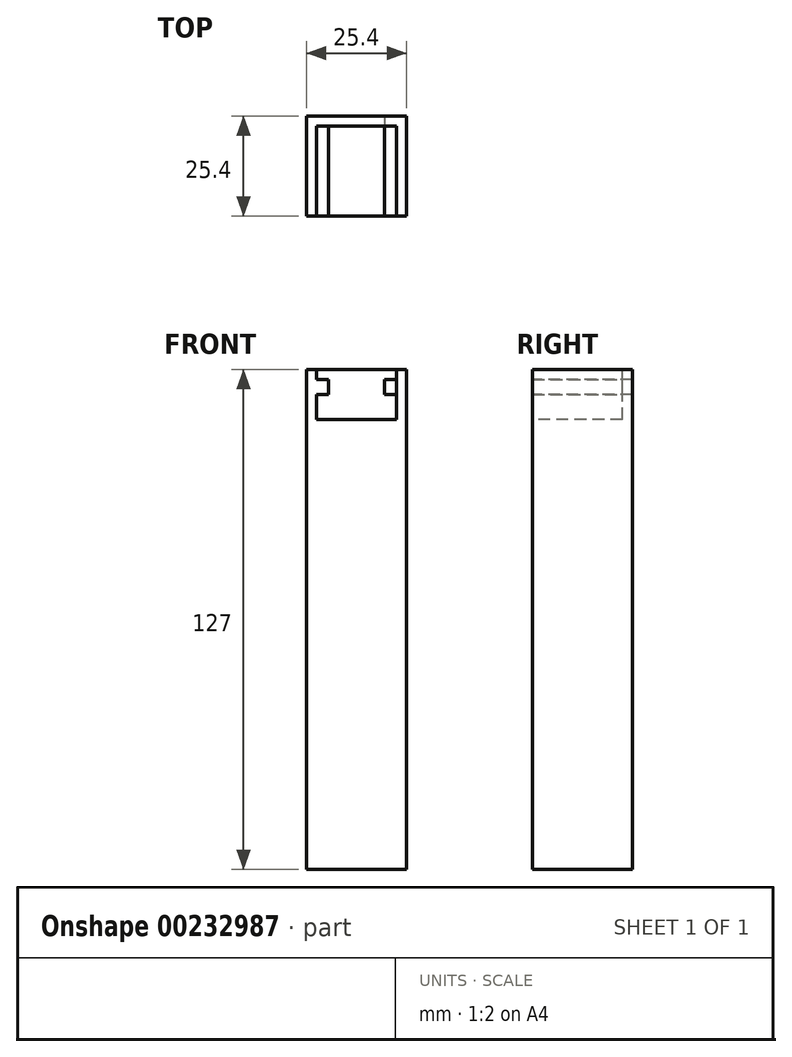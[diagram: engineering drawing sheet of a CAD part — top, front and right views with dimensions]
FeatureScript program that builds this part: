
annotation { "Feature Type Name" : "Feature", "Feature Type Description" : "" }
export const myFeature = defineFeature(function(context is Context, id is Id, definition is map)
    precondition{}
    {
        {
            var Q0;
            Q0=qCreatedBy(makeId("Top.planeOp"),FACE);
            var sketch = newSketch(context, id + "F0", { "sketchPlane" : qUnion([Q0])});
            skLineSegment(sketch, "E0.bottom", {"start": v(0, 0) * mm, "end": v(25.4, 0) * mm});
            skLineSegment(sketch, "E0.top", {"start": v(0, 25.4) * mm, "end": v(25.4, 25.4) * mm});
            skLineSegment(sketch, "E0.left", {"start": v(0, 0) * mm, "end": v(0, 25.4) * mm});
            skLineSegment(sketch, "E0.right", {"start": v(25.4, 0) * mm, "end": v(25.4, 25.4) * mm});
            skSolve(sketch);
        }
        {
            var Q0;
            Q0=makeQuery(id+"F0.imprint","IMPRINT",FACE,{"disambiguationData":[TD([[makeQuery(id+"F0.imprint","IMPRINT",EDGE,{"derivedFrom":sQuery(id+"F0.wireOp",EDGE,"E0.bottom")}),1.0]])]});
            extrude(context, id + "F1", {"entities" : qUnion([Q0]), "oppositeDirection" : true, "depth" : 127 * mm});
        }
        {
            var Q0;
            Q0=makeQuery(id+"F1.opExtrude","CAP_FACE",FACE,{"disambiguationData":[OSD([sQuery(id+"F0.wireOp",EDGE,"E0.bottom"),sQuery(id+"F0.wireOp",EDGE,"E0.top"),sQuery(id+"F0.wireOp",EDGE,"E0.left"),sQuery(id+"F0.wireOp",EDGE,"E0.right")])],"isStart":true});
            var sketch = newSketch(context, id + "F2", { "sketchPlane" : qUnion([Q0])});
            skLineSegment(sketch, "E1.bottom", {"start": v(2.54, 22.86) * mm, "end": v(22.86, 22.86) * mm});
            skLineSegment(sketch, "E1.top", {"start": v(2.54, 0) * mm, "end": v(22.86, 0) * mm});
            skLineSegment(sketch, "E1.left", {"start": v(2.54, 22.86) * mm, "end": v(2.54, 0) * mm});
            skLineSegment(sketch, "E1.right", {"start": v(22.86, 22.86) * mm, "end": v(22.86, 0) * mm});
            skSolve(sketch);
        }
        {
            var Q0;
            Q0=makeQuery(id+"F2.imprint","IMPRINT",FACE,{"disambiguationData":[TD([[makeQuery(id+"F2.imprint","IMPRINT",EDGE,{"derivedFrom":sQuery(id+"F2.wireOp",EDGE,"E1.bottom")}),-1.0]])]});
            extrude(context, id + "F3", {"entities" : qUnion([Q0]), "operationType" : NewBodyOperationType.REMOVE, "oppositeDirection" : true, "depth" : 12.7 * mm});
        }
        {
            var Q0;
            Q0=makeQuery(id+"F3.boolean.opBoolean","COPY",FACE,{"derivedFrom":makeQuery(id+"F3.opExtrude","SWEPT_FACE",FACE,{"disambiguationData":[OSD([sQuery(id+"F2.wireOp",EDGE,"E1.left")])]})});
            var sketch = newSketch(context, id + "F4", { "sketchPlane" : qUnion([Q0])});
            skLineSegment(sketch, "E2.bottom", {"start": v(0, -2.54) * mm, "end": v(22.86, -2.54) * mm});
            skLineSegment(sketch, "E2.top", {"start": v(0, -6.35) * mm, "end": v(22.86, -6.35) * mm});
            skLineSegment(sketch, "E2.left", {"start": v(0, -2.54) * mm, "end": v(0, -6.35) * mm});
            skLineSegment(sketch, "E2.right", {"start": v(22.86, -2.54) * mm, "end": v(22.86, -6.35) * mm});
            skSolve(sketch);
        }
        {
            var Q0;
            Q0=makeQuery(id+"F4.imprint","IMPRINT",FACE,{"disambiguationData":[TD([[makeQuery(id+"F4.imprint","IMPRINT",EDGE,{"derivedFrom":sQuery(id+"F4.wireOp",EDGE,"E2.bottom")}),-1.0]])]});
            extrude(context, id + "F5", {"entities" : qUnion([Q0]), "operationType" : NewBodyOperationType.ADD, "depth" : 3.05 * mm});
        }
        {
            var Q0;
            Q0=makeQuery(id+"F5.boolean.opBoolean","MERGE",FACE,{"derivedFrom":[makeQuery(id+"F1.opExtrude","SWEPT_FACE",FACE,{"disambiguationData":[OSD([sQuery(id+"F0.wireOp",EDGE,"E0.bottom")])]}),makeQuery(id+"F5.opExtrude","SWEPT_FACE",FACE,{"disambiguationData":[OSD([sQuery(id+"F4.wireOp",EDGE,"E2.left")])]})]});
            var sketch = newSketch(context, id + "F6", { "sketchPlane" : qUnion([Q0])});
            skLineSegment(sketch, "E3.bottom", {"start": v(22.86, -2.54) * mm, "end": v(19.81, -2.54) * mm});
            skLineSegment(sketch, "E3.top", {"start": v(22.86, -6.35) * mm, "end": v(19.81, -6.35) * mm});
            skLineSegment(sketch, "E3.left", {"start": v(22.86, -2.54) * mm, "end": v(22.86, -6.35) * mm});
            skLineSegment(sketch, "E3.right", {"start": v(19.81, -2.54) * mm, "end": v(19.81, -6.35) * mm});
            skSolve(sketch);
        }
        {
            var Q0;
            Q0=makeQuery(id+"F6.imprint","IMPRINT",FACE,{"disambiguationData":[TD([[makeQuery(id+"F6.imprint","IMPRINT",EDGE,{"derivedFrom":sQuery(id+"F6.wireOp",EDGE,"E3.bottom")}),1.0]])]});
            extrude(context, id + "F7", {"entities" : qUnion([Q0]), "oppositeDirection" : true, "depth" : 25.4 * mm});
        }
    });
